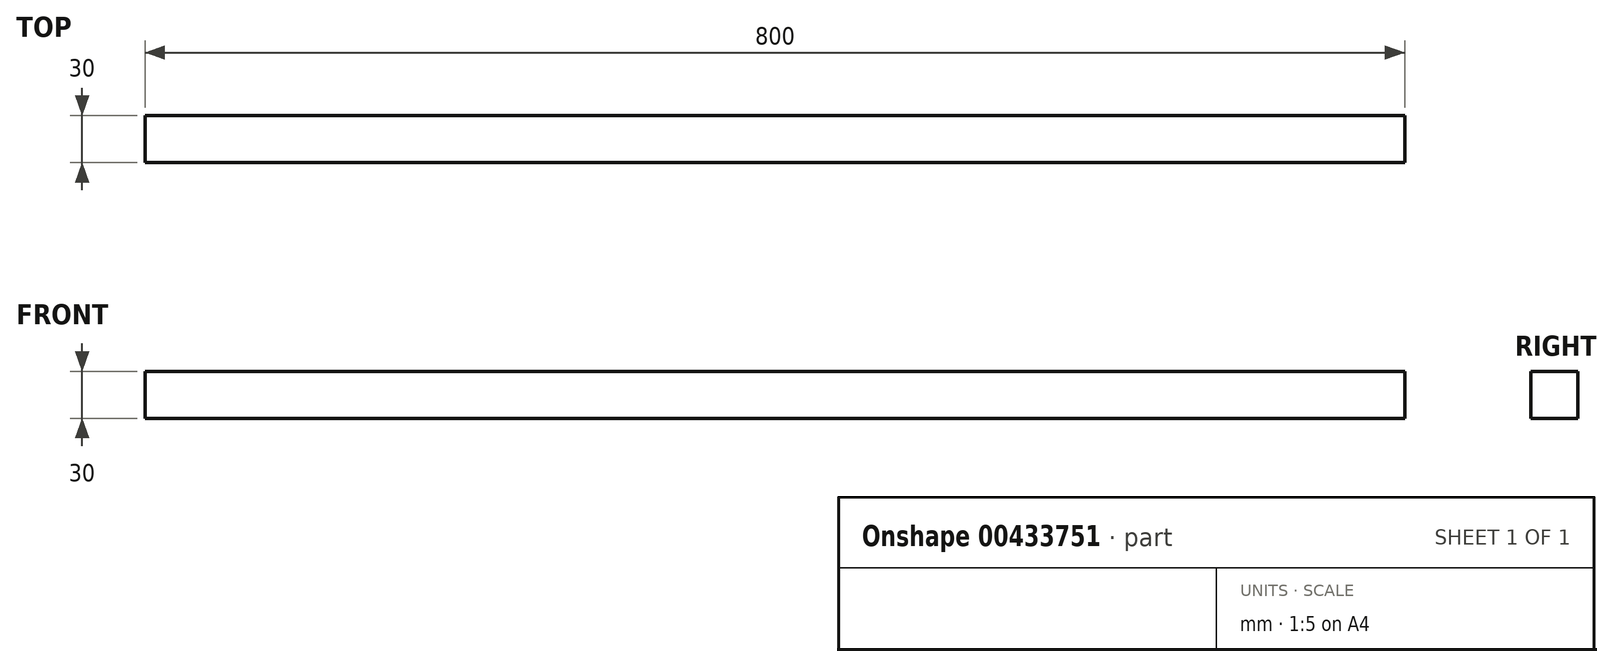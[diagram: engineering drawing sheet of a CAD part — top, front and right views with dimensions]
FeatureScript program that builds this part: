
annotation { "Feature Type Name" : "Feature", "Feature Type Description" : "" }
export const myFeature = defineFeature(function(context is Context, id is Id, definition is map)
    precondition{}
    {
        {
            var Q0;
            Q0=qCreatedBy(makeId("Front.planeOp"),FACE);
            var sketch = newSketch(context, id + "F0", { "sketchPlane" : qUnion([Q0])});
            skLineSegment(sketch, "E0.bottom", {"start": v(-430.04, -89.16) * mm, "end": v(369.96, -89.16) * mm});
            skLineSegment(sketch, "E0.top", {"start": v(-430.04, -119.16) * mm, "end": v(369.96, -119.16) * mm});
            skLineSegment(sketch, "E0.left", {"start": v(-430.04, -89.16) * mm, "end": v(-430.04, -119.16) * mm});
            skLineSegment(sketch, "E0.right", {"start": v(369.96, -89.16) * mm, "end": v(369.96, -119.16) * mm});
            skSolve(sketch);
        }
        {
            var Q0;
            Q0 = qSketchRegion(id + "F0", true);
            extrude(context, id + "F1", {"entities" : qUnion([Q0]), "depth" : 30 * mm, "offsetDistance" : 25 * mm});
        }
    });
